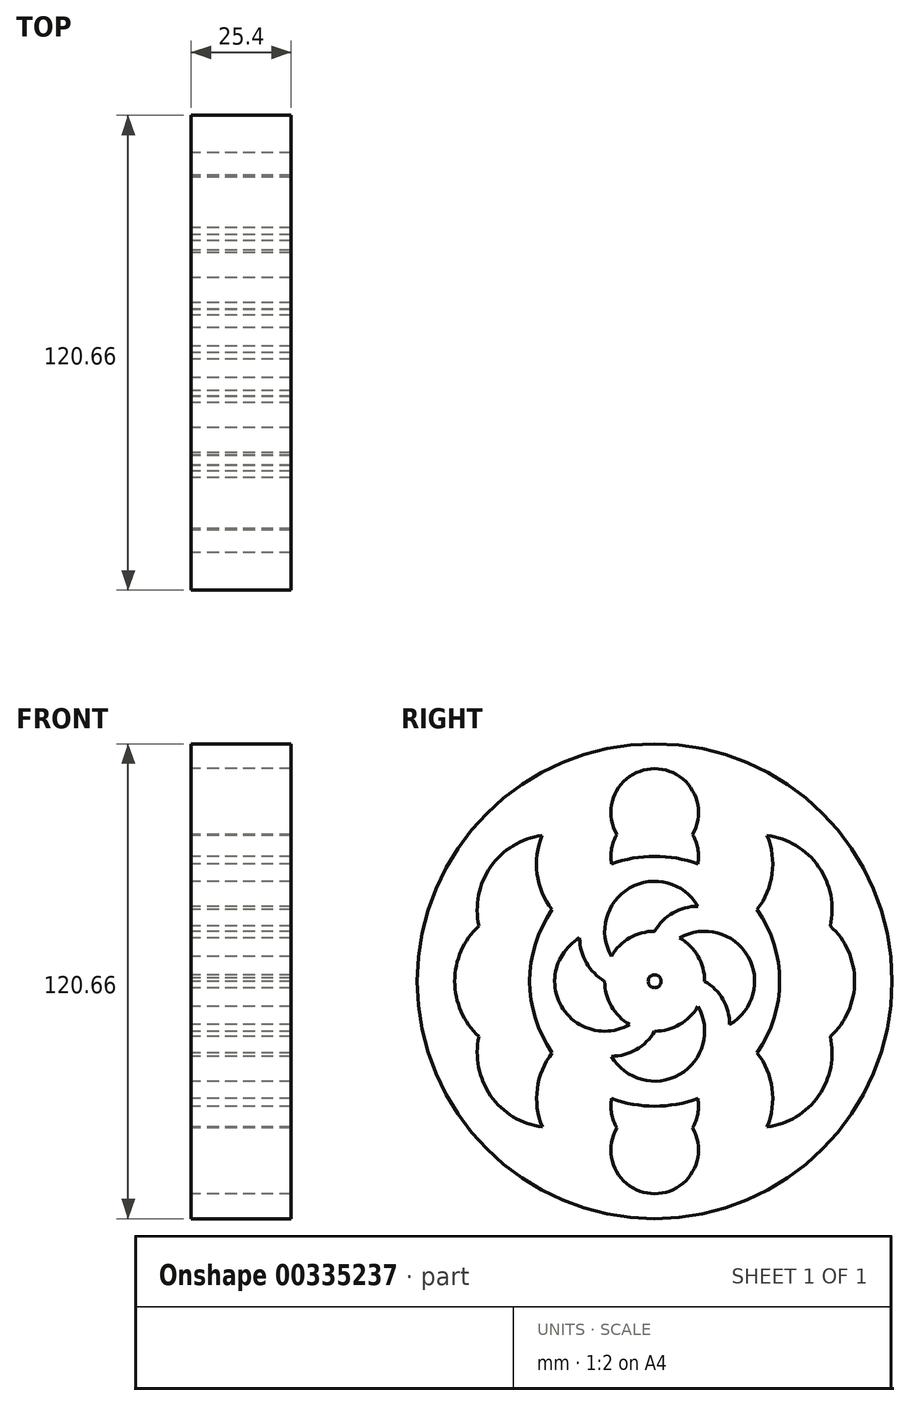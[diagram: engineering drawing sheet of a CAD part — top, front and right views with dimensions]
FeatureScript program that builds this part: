
annotation { "Feature Type Name" : "Feature", "Feature Type Description" : "" }
export const myFeature = defineFeature(function(context is Context, id is Id, definition is map)
    precondition{}
    {
        {
            var Q0;
            Q0=qCreatedBy(makeId("Right.planeOp"),FACE);
            var sketch = newSketch(context, id + "F0", { "sketchPlane" : qUnion([Q0])});
            skCircle(sketch, "E0", {"center": v(0, 0) * mm, "radius": 60.33 * mm});
            skCircle(sketch, "E1", {"center": v(0, 0) * mm, "radius": 1.65 * mm});
            skArc(sketch, "E2", {"start": v(-12.7, 0) * mm, "mid": v(-11, -6.35) * mm, "end": v(-6.35, -11) * mm});
            skArc(sketch, "E3", {"start": v(-25.39, 0.87) * mm, "mid": v(-25.4, 0.43) * mm, "end": v(-25.4, 0) * mm});
            skArc(sketch, "E4", {"start": v(11, 19.05) * mm, "mid": v(-6.35, 23.7) * mm, "end": v(-11, 6.35) * mm});
            skArc(sketch, "E5", {"start": v(11, 19.05) * mm, "mid": v(4.65, 17.35) * mm, "end": v(0, 12.7) * mm});
            skArc(sketch, "E6.trimOffspring", {"start": v(19.05, -11) * mm, "mid": v(23.7, 6.35) * mm, "end": v(6.35, 11) * mm});
            skArc(sketch, "E7.trimOffspring", {"start": v(19.05, -11) * mm, "mid": v(17.35, -4.65) * mm, "end": v(12.7, 0) * mm});
            skArc(sketch, "E8", {"start": v(-19.05, 11) * mm, "mid": v(-23.7, -6.35) * mm, "end": v(-6.35, -11) * mm});
            skArc(sketch, "E9", {"start": v(-19.05, 11) * mm, "mid": v(-17.35, 4.65) * mm, "end": v(-12.7, 0) * mm});
            skArc(sketch, "E10", {"start": v(-11, -19.05) * mm, "mid": v(6.35, -23.7) * mm, "end": v(11, -6.35) * mm});
            skArc(sketch, "E11.trimOffspring", {"start": v(-11, -19.05) * mm, "mid": v(-4.65, -17.35) * mm, "end": v(0, -12.7) * mm});
            skArc(sketch, "E12.trimOffspring", {"start": v(0, 12.7) * mm, "mid": v(-6.35, 11) * mm, "end": v(-11, 6.35) * mm});
            skArc(sketch, "E13.trimOffspring", {"start": v(12.7, 0) * mm, "mid": v(11, 6.35) * mm, "end": v(6.35, 11) * mm});
            skArc(sketch, "E14.trimOffspring", {"start": v(0, -12.7) * mm, "mid": v(6.35, -11) * mm, "end": v(11, -6.35) * mm});
            skArc(sketch, "E15", {"start": v(26.04, -18.17) * mm, "mid": v(31.75, 0) * mm, "end": v(26.03, 18.17) * mm});
            skArc(sketch, "E16", {"start": v(-44.63, 14.04) * mm, "mid": v(-50.8, 0) * mm, "end": v(-44.63, -14.04) * mm});
            skArc(sketch, "E17", {"start": v(-28.6, 37.05) * mm, "mid": v(-41.67, 29.06) * mm, "end": v(-44.63, 14.04) * mm});
            skArc(sketch, "E18", {"start": v(-28.6, 37.05) * mm, "mid": v(-29.88, 27.25) * mm, "end": v(-26.07, 18.13) * mm});
            skArc(sketch, "E19.trimOffspring", {"start": v(-26.03, 18.17) * mm, "mid": v(-26.08, 18.19) * mm, "end": v(-26.12, 18.2) * mm});
            skArc(sketch, "E20", {"start": v(-25.37, 0.87) * mm, "mid": v(-25.38, 0.87) * mm, "end": v(-25.39, 0.87) * mm});
            skArc(sketch, "E21", {"start": v(-26.04, -18.17) * mm, "mid": v(-29.83, -27.27) * mm, "end": v(-28.56, -37.05) * mm});
            skArc(sketch, "E22.trimOffspring", {"start": v(-44.63, -14.04) * mm, "mid": v(-41.66, -29.08) * mm, "end": v(-28.56, -37.05) * mm});
            skArc(sketch, "E23", {"start": v(44.63, -14.04) * mm, "mid": v(50.8, 0) * mm, "end": v(44.63, 14.04) * mm});
            skArc(sketch, "E24.trimOffspring", {"start": v(26.03, 18.17) * mm, "mid": v(29.83, 27.27) * mm, "end": v(28.56, 37.05) * mm});
            skArc(sketch, "E25.trimOffspring", {"start": v(44.63, 14.04) * mm, "mid": v(41.66, 29.08) * mm, "end": v(28.56, 37.05) * mm});
            skArc(sketch, "E26", {"start": v(28.56, -37.05) * mm, "mid": v(41.66, -29.08) * mm, "end": v(44.63, -14.04) * mm});
            skArc(sketch, "E27", {"start": v(28.56, -37.05) * mm, "mid": v(29.83, -27.27) * mm, "end": v(26.03, -18.17) * mm});
            skArc(sketch, "E28.trimOffspring", {"start": v(-26.04, 18.17) * mm, "mid": v(-26.05, 18.15) * mm, "end": v(-26.07, 18.13) * mm});
            skArc(sketch, "E29", {"start": v(-26.03, 18.17) * mm, "mid": v(-31.75, 0) * mm, "end": v(-26.03, -18.17) * mm});
            skArc(sketch, "E30.trimOffspring", {"start": v(10.95, 29.8) * mm, "mid": v(-0.03, 31.75) * mm, "end": v(-11, 29.78) * mm});
            skLineSegment(sketch, "E31", {"start": v(0, 60.33) * mm, "end": v(0, -60.33) * mm, "construction": true});
            skArc(sketch, "E32", {"start": v(10.95, 29.8) * mm, "mid": v(10.95, 33.67) * mm, "end": v(9.63, 37.3) * mm});
            skArc(sketch, "E33", {"start": v(-10.95, -29.8) * mm, "mid": v(-10.95, -33.67) * mm, "end": v(-9.63, -37.3) * mm});
            skArc(sketch, "E34.trimOffspring", {"start": v(-10.95, -29.8) * mm, "mid": v(0, -31.75) * mm, "end": v(10.95, -29.8) * mm});
            skArc(sketch, "E35", {"start": v(-9.63, -37.3) * mm, "mid": v(0, -53.99) * mm, "end": v(9.63, -37.3) * mm});
            skArc(sketch, "E36", {"start": v(9.63, 37.3) * mm, "mid": v(0, 53.99) * mm, "end": v(-9.63, 37.3) * mm});
            skArc(sketch, "E37.trimOffspring", {"start": v(-9.63, 37.3) * mm, "mid": v(-10.95, 33.67) * mm, "end": v(-10.95, 29.8) * mm});
            skArc(sketch, "E38.trimOffspring", {"start": v(9.63, -37.3) * mm, "mid": v(10.95, -33.67) * mm, "end": v(10.95, -29.8) * mm});
            skSolve(sketch);
        }
        {
            var Q0;
            Q0=makeQuery(id+"F0.imprint","IMPRINT",FACE,{"disambiguationData":[TD([[makeQuery(id+"F0.imprint","IMPRINT",EDGE,{"derivedFrom":sQuery(id+"F0.wireOp",EDGE,"E0")}),1.0]])]});
            var Q1;
            {var subQ0=sQuery(id+"F0.wireOp",EDGE,"E5");Q1=makeQuery(id+"F0.imprint","IMPRINT",FACE,{"disambiguationData":[TD([[makeQuery(id+"F0.imprint","IMPRINT",EDGE,{"derivedFrom":subQ0}),1.0]])]});}
            var Q2;
            {var subQ8=sQuery(id+"F0.wireOp",EDGE,"f1aad0b1-0add-4b22-8ff7-48d8023dbe04.trimOffspring");var subQ9=sQuery(id+"F0.wireOp",EDGE,"E1");var subQ10=makeQuery(id+"F0.imprint","INTERSECT",VERTEX,{"disambiguationData":[OD(1.0)],"derivedFrom":[subQ9,subQ8]});Q2=makeQuery(id+"F0.imprint","IMPRINT",FACE,{"disambiguationData":[TD([[makeQuery(id+"F0.imprint","IMPRINT",EDGE,{"disambiguationData":[TD([[subQ10,-1.0]])],"derivedFrom":subQ9}),-1.0]])]});}
            var Q3;
            {var subQ0=sQuery(id+"F0.wireOp",EDGE,"E9");Q3=makeQuery(id+"F0.imprint","IMPRINT",FACE,{"disambiguationData":[TD([[makeQuery(id+"F0.imprint","IMPRINT",EDGE,{"derivedFrom":subQ0}),1.0]])]});}
            var Q4;
            {var subQ0=sQuery(id+"F0.wireOp",EDGE,"E11.trimOffspring");Q4=makeQuery(id+"F0.imprint","IMPRINT",FACE,{"disambiguationData":[TD([[makeQuery(id+"F0.imprint","IMPRINT",EDGE,{"derivedFrom":subQ0}),1.0]])]});}
            var Q5;
            {var subQ0=sQuery(id+"F0.wireOp",EDGE,"E7.trimOffspring");Q5=makeQuery(id+"F0.imprint","IMPRINT",FACE,{"disambiguationData":[TD([[makeQuery(id+"F0.imprint","IMPRINT",EDGE,{"derivedFrom":subQ0}),1.0]])]});}
            extrude(context, id + "F1", {"entities" : qUnion([Q0, Q1, Q2, Q3, Q4, Q5]), "depth" : 25.4 * mm});
        }
    });
